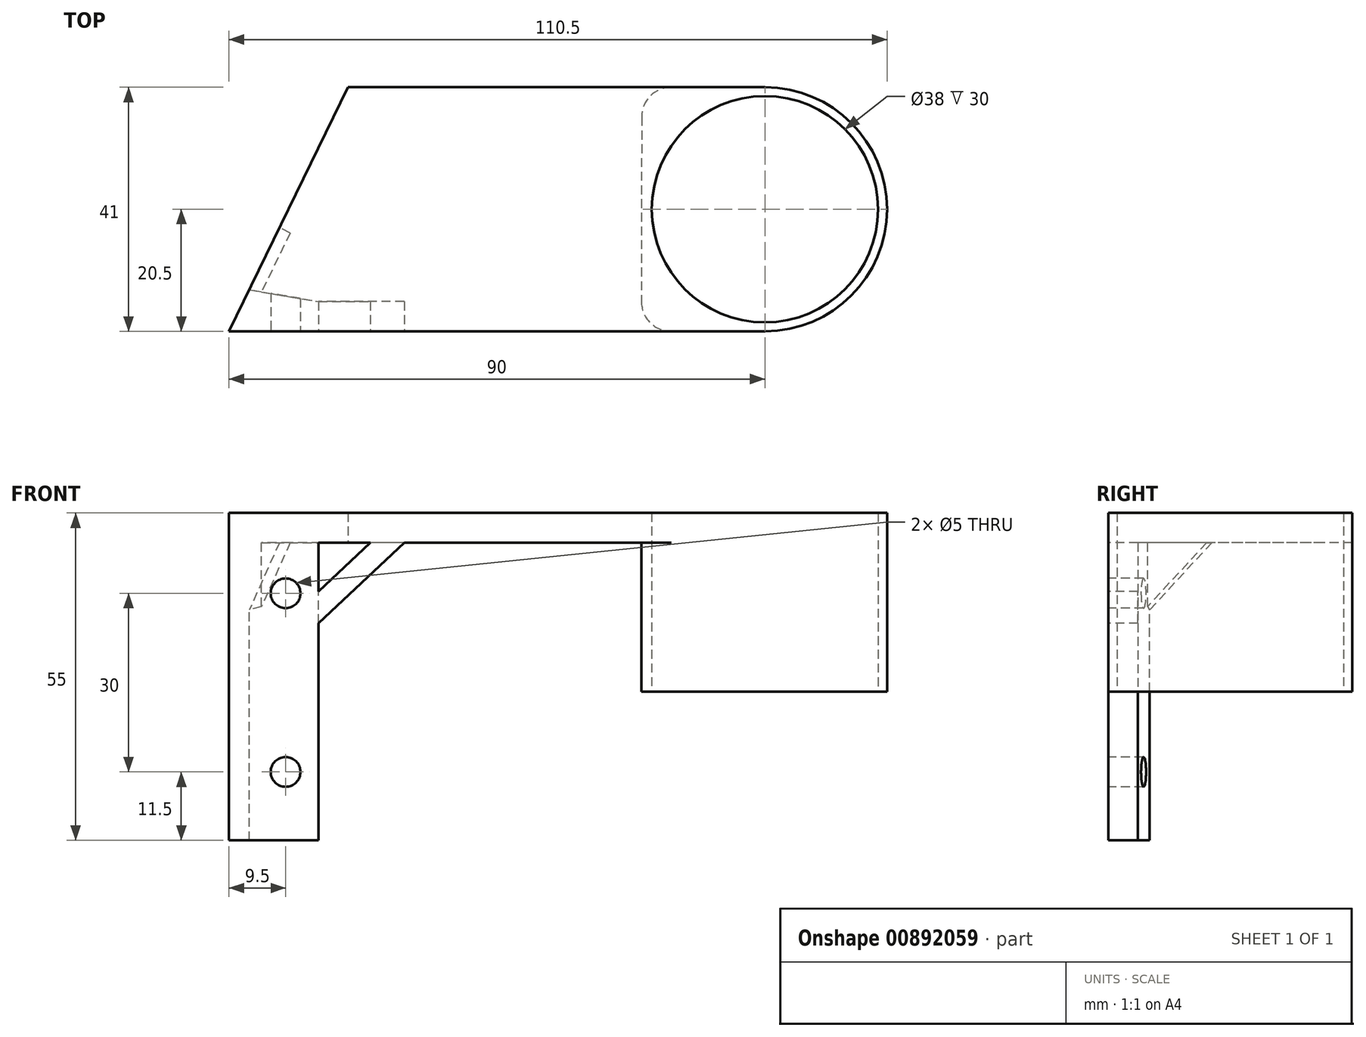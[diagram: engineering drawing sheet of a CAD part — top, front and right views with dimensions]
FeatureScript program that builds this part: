
annotation { "Feature Type Name" : "Feature", "Feature Type Description" : "" }
export const myFeature = defineFeature(function(context is Context, id is Id, definition is map)
    precondition{}
    {
        {
            var Q0;
            Q0=qCreatedBy(makeId("Top.planeOp"),FACE);
            var sketch = newSketch(context, id + "F0", { "sketchPlane" : qUnion([Q0])});
            skCircle(sketch, "E0", {"center": v(0, 0) * mm, "radius": 20.5 * mm});
            skCircle(sketch, "E1", {"center": v(0, 0) * mm, "radius": 19 * mm});
            skLineSegment(sketch, "E2", {"start": v(0, 0) * mm, "end": v(0, 20.5) * mm});
            skLineSegment(sketch, "E3", {"start": v(0, 20.5) * mm, "end": v(-70, 20.5) * mm});
            skLineSegment(sketch, "E4", {"start": v(0, -20.5) * mm, "end": v(-90, -20.5) * mm});
            skLineSegment(sketch, "E5", {"start": v(-70, 20.5) * mm, "end": v(-90, -20.5) * mm});
            skSolve(sketch);
        }
        {
            var Q0;
            Q0=qSketchRegion(id+"F0",true);
            extrude(context, id + "F1", {"entities" : qUnion([Q0]), "depth" : 55 * mm, "offsetDistance" : 25 * mm});
        }
        {
            var Q0;
            {var subQ0=sQuery(id+"F0.wireOp",EDGE,"E3");Q0=makeQuery(id+"F0.imprint","IMPRINT",FACE,{"disambiguationData":[TD([[makeQuery(id+"F0.imprint","IMPRINT",EDGE,{"derivedFrom":subQ0}),1.0]])]});}
            var sketch = newSketch(context, id + "F2", { "sketchPlane" : qUnion([Q0])});
            skLineSegment(sketch, "E6", {"start": v(-92.3, 24.13) * mm, "end": v(-20.7, 24.13) * mm});
            skLineSegment(sketch, "E7", {"start": v(-92.68, -12.5) * mm, "end": v(-92.3, 24.13) * mm});
            skLineSegment(sketch, "E8", {"start": v(-75, -15.5) * mm, "end": v(-75, -22) * mm});
            skLineSegment(sketch, "E9", {"start": v(-75, -22) * mm, "end": v(-20.75, -22) * mm});
            skLineSegment(sketch, "E10", {"start": v(-20.7, 24.13) * mm, "end": v(-20.75, -22) * mm});
            skLineSegment(sketch, "E11", {"start": v(-92.68, -12.5) * mm, "end": v(-75, -15.5) * mm});
            skSolve(sketch);
        }
        {
            var Q0;
            Q0=qSketchRegion(id+"F2",true);
            extrude(context, id + "F3", {"entities" : qUnion([Q0]), "operationType" : NewBodyOperationType.REMOVE, "depth" : 50 * mm, "offsetDistance" : 25 * mm});
        }
        {
            var Q0;
            {var subQ0=sQuery(id+"F2.wireOp",EDGE,"E10");var subQ1=sQuery(id+"F0.wireOp",EDGE,"E3");var subQ2=makeQuery(id+"F0.imprint","IMPRINT",EDGE,{"derivedFrom":subQ1});var subQ3=makeQuery(id+"F2.imprint","INTERSECT",VERTEX,{"derivedFrom":[subQ2,subQ0]});Q0=makeQuery(id+"F2.imprint","IMPRINT",FACE,{"disambiguationData":[TD([[makeQuery(id+"F2.imprint","IMPRINT",EDGE,{"disambiguationData":[TD([[subQ3,-1.0]])],"derivedFrom":subQ0}),1.0]])]});}
            var sketch = newSketch(context, id + "F4", { "sketchPlane" : qUnion([Q0])});
            skLineSegment(sketch, "E12.bottom", {"start": v(-24.09, -27.18) * mm, "end": v(22.58, -27.18) * mm});
            skLineSegment(sketch, "E12.top", {"start": v(-24.09, 30.66) * mm, "end": v(22.58, 30.66) * mm});
            skLineSegment(sketch, "E12.left", {"start": v(-24.09, -27.18) * mm, "end": v(-24.09, 30.66) * mm});
            skLineSegment(sketch, "E12.right", {"start": v(22.58, -27.18) * mm, "end": v(22.58, 30.66) * mm});
            skSolve(sketch);
        }
        {
            var Q0;
            Q0=qSketchRegion(id+"F4",true);
            extrude(context, id + "F5", {"entities" : qUnion([Q0]), "operationType" : NewBodyOperationType.REMOVE, "depth" : 25 * mm, "offsetDistance" : 25 * mm});
        }
        {
            var Q0;
            Q0=makeQuery(id+"F3.boolean.opBoolean","INTERSECT",EDGE,{"derivedFrom":[makeQuery(id+"F1.opExtrude","SWEPT_FACE",FACE,{"disambiguationData":[OSD([sQuery(id+"F0.wireOp",EDGE,"E3")])]}),makeQuery(id+"F3.opExtrude","SWEPT_FACE",FACE,{"disambiguationData":[OSD([sQuery(id+"F2.wireOp",EDGE,"E10")])]})]});
            var Q1;
            Q1=makeQuery(id+"F3.boolean.opBoolean","INTERSECT",EDGE,{"derivedFrom":[makeQuery(id+"F1.opExtrude","SWEPT_FACE",FACE,{"disambiguationData":[OSD([sQuery(id+"F0.wireOp",EDGE,"E4")])]}),makeQuery(id+"F3.opExtrude","SWEPT_FACE",FACE,{"disambiguationData":[OSD([sQuery(id+"F2.wireOp",EDGE,"E10")])]})]});
            fillet(context, id + "F6", {"entities" : qUnion([Q0, Q1]), "radius" : 5 * mm, "tangentPropagation" : true, "allowEdgeOverflow" : false});
        }
        {
            var Q0;
            Q0=makeQuery(id+"F1.opExtrude","SWEPT_FACE",FACE,{"disambiguationData":[OSD([sQuery(id+"F0.wireOp",EDGE,"E4")])]});
            var sketch = newSketch(context, id + "F7", { "sketchPlane" : qUnion([Q0])});
            skPoint(sketch, "E13", {"position": v(-80.5, 41.5) * mm});
            skPoint(sketch, "E14", {"position": v(-80.5, 11.5) * mm});
            skSolve(sketch);
        }
        {
            var Q0;
            Q0=sQuery(id+"F7.wireOp",VERTEX,"E13");
            var Q1;
            Q1=sQuery(id+"F7.wireOp",VERTEX,"E14");
            var Q2;
            Q2=makeQuery(id+"F1.opExtrude","SWEPT_BODY",BODY,{"disambiguationData":[OSD([sQuery(id+"F0.wireOp",EDGE,"E0"),sQuery(id+"F0.wireOp",EDGE,"E1"),sQuery(id+"F0.wireOp",EDGE,"E3"),sQuery(id+"F0.wireOp",EDGE,"E4"),sQuery(id+"F0.wireOp",EDGE,"E5")])]});
            hole(context, id + "F8", {"style" : HoleStyle.SIMPLE, "endStyle" : HoleEndStyle.THROUGH, "holeDiameter" : 5 * mm, "majorDiameter" : 5 * mm, "isTappedThrough" : true, "tappedDepth" : 12 * mm, "tapClearance" : 3, "locations" : qUnion([Q0, Q1]), "scope" : qUnion([Q2])});
        }
        {
            var Q0;
            Q0=makeQuery(id+"F1.opExtrude","SWEPT_FACE",FACE,{"disambiguationData":[OSD([sQuery(id+"F0.wireOp",EDGE,"E4")])]});
            var sketch = newSketch(context, id + "F9", { "sketchPlane" : qUnion([Q0])});
            skLineSegment(sketch, "E15", {"start": v(-76.33, 40.55) * mm, "end": v(-63.36, 52.71) * mm});
            skLineSegment(sketch, "E16", {"start": v(-63.36, 52.71) * mm, "end": v(-57.68, 52.71) * mm});
            skLineSegment(sketch, "E17", {"start": v(-57.68, 52.71) * mm, "end": v(-76.67, 34.91) * mm});
            skLineSegment(sketch, "E18", {"start": v(-76.67, 34.91) * mm, "end": v(-76.33, 40.55) * mm});
            skSolve(sketch);
        }
        {
            var Q0;
            {var subQ1=sQuery(id+"F2.wireOp",EDGE,"E8");var subQ2=makeQuery(id+"F1.opExtrude","SWEPT_FACE",FACE,{"disambiguationData":[OSD([sQuery(id+"F0.wireOp",EDGE,"E4")])]});var subQ3=makeQuery(id+"F3.boolean.opBoolean","INTERSECT",EDGE,{"derivedFrom":[subQ2,makeQuery(id+"F3.opExtrude","SWEPT_FACE",FACE,{"disambiguationData":[OSD([subQ1])]})]});var subQ7=sQuery(id+"F9.wireOp",EDGE,"E17");var subQ9=makeQuery(id+"F9.imprint","INTERSECT",VERTEX,{"derivedFrom":[subQ3,subQ7]});Q0=makeQuery(id+"F9.imprint","IMPRINT",FACE,{"disambiguationData":[TD([[makeQuery(id+"F9.imprint","IMPRINT",EDGE,{"disambiguationData":[TD([[subQ9,-1.0]])],"derivedFrom":subQ3}),-1.0]])]});}
            extrude(context, id + "F10", {"entities" : qUnion([Q0]), "operationType" : NewBodyOperationType.ADD, "oppositeDirection" : true, "depth" : 5 * mm, "offsetDistance" : 25 * mm});
        }
        {
            var Q0;
            Q0=makeQuery(id+"F1.opExtrude","SWEPT_FACE",FACE,{"disambiguationData":[OSD([sQuery(id+"F0.wireOp",EDGE,"E5")])]});
            var sketch = newSketch(context, id + "F11", { "sketchPlane" : qUnion([Q0])});
            skLineSegment(sketch, "E19", {"start": v(35.9, 52.56) * mm, "end": v(52.58, 36.33) * mm});
            skLineSegment(sketch, "E20", {"start": v(52.58, 36.33) * mm, "end": v(52.58, 43.17) * mm});
            skLineSegment(sketch, "E21", {"start": v(52.58, 43.17) * mm, "end": v(52.58, 52.5) * mm});
            skLineSegment(sketch, "E22", {"start": v(52.58, 52.5) * mm, "end": v(35.9, 52.56) * mm});
            skSolve(sketch);
        }
        {
            var Q0;
            {var subQ0=sQuery(id+"F11.wireOp",EDGE,"E19");var subQ1=sQuery(id+"F2.wireOp",EDGE,"E11");var subQ2=makeQuery(id+"F1.opExtrude","SWEPT_FACE",FACE,{"disambiguationData":[OSD([sQuery(id+"F0.wireOp",EDGE,"E5")])]});var subQ5=makeQuery(id+"F3.boolean.opBoolean","INTERSECT",EDGE,{"derivedFrom":[subQ2,makeQuery(id+"F3.opExtrude","SWEPT_FACE",FACE,{"disambiguationData":[OSD([subQ1])]})]});var subQ6=makeQuery(id+"F11.imprint","INTERSECT",VERTEX,{"derivedFrom":[subQ5,subQ0]});Q0=makeQuery(id+"F11.imprint","IMPRINT",FACE,{"disambiguationData":[TD([[makeQuery(id+"F11.imprint","IMPRINT",EDGE,{"disambiguationData":[TD([[subQ6,1.0]])],"derivedFrom":subQ0}),1.0]])]});}
            extrude(context, id + "F12", {"entities" : qUnion([Q0]), "operationType" : NewBodyOperationType.ADD, "oppositeDirection" : true, "depth" : 2 * mm, "offsetDistance" : 25 * mm});
        }
    });
